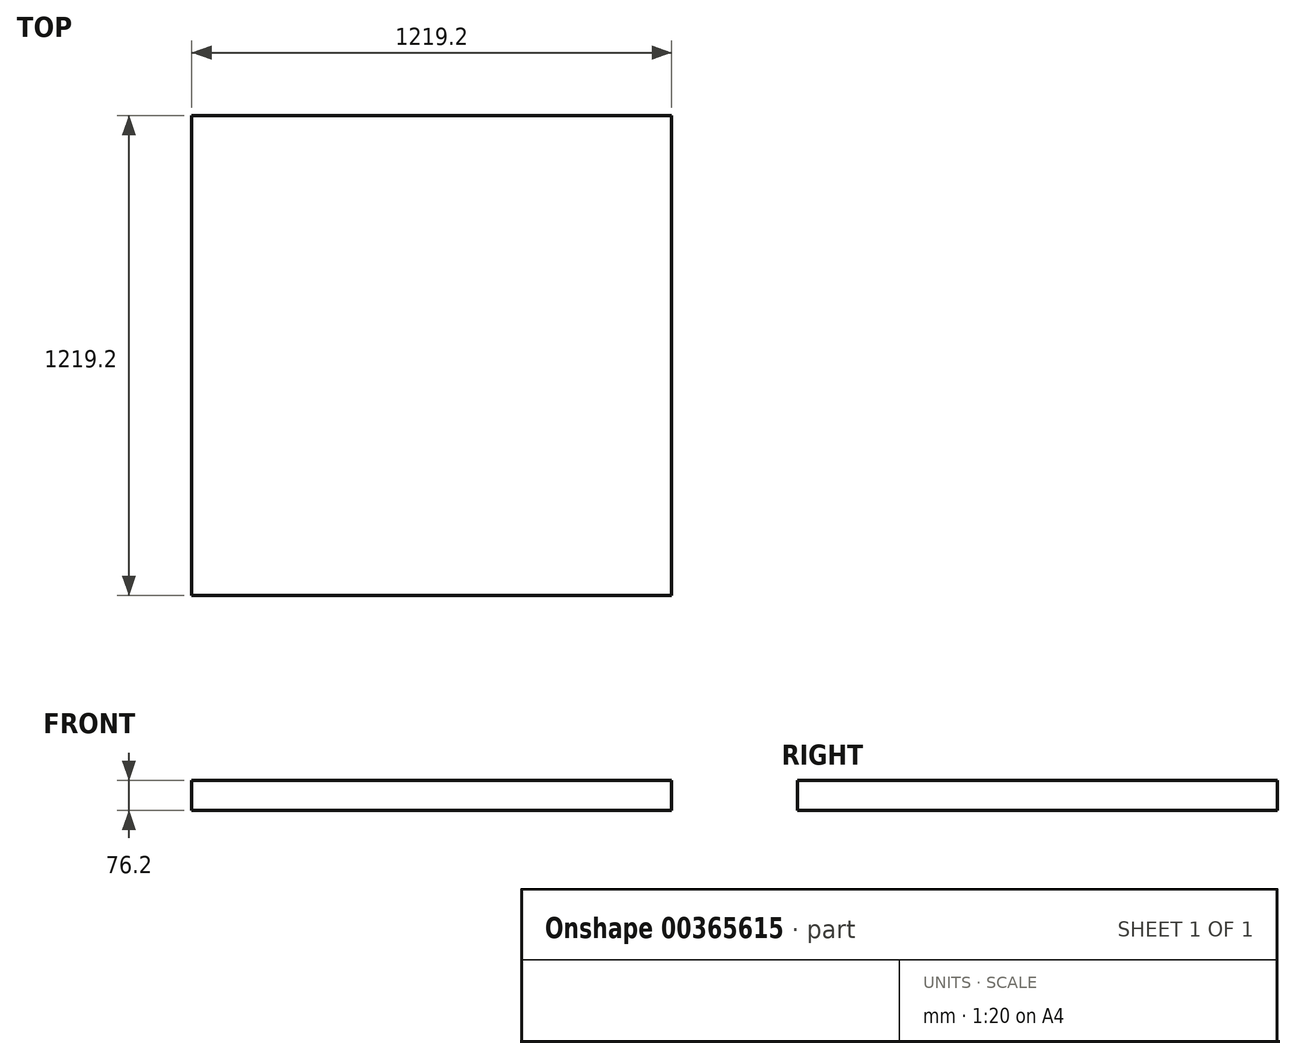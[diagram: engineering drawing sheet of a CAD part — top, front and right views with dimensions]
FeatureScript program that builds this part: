
annotation { "Feature Type Name" : "Feature", "Feature Type Description" : "" }
export const myFeature = defineFeature(function(context is Context, id is Id, definition is map)
    precondition{}
    {
        {
            var Q0;
            Q0=qCreatedBy(makeId("Top.planeOp"),FACE);
            var sketch = newSketch(context, id + "F0", { "sketchPlane" : qUnion([Q0])});
            skLineSegment(sketch, "E0.bottom", {"start": v(609.6, -609.6) * mm, "end": v(-609.6, -609.6) * mm});
            skLineSegment(sketch, "E0.top", {"start": v(609.6, 609.6) * mm, "end": v(-609.6, 609.6) * mm});
            skLineSegment(sketch, "E0.left", {"start": v(609.6, -609.6) * mm, "end": v(609.6, 609.6) * mm});
            skLineSegment(sketch, "E0.right", {"start": v(-609.6, -609.6) * mm, "end": v(-609.6, 609.6) * mm});
            skPoint(sketch, "E0.middle", {"position": v(0, 0) * mm});
            skSolve(sketch);
        }
        {
            var Q0;
            Q0=makeQuery(id+"F0.imprint","IMPRINT",FACE,{"disambiguationData":[TD([[makeQuery(id+"F0.imprint","IMPRINT",EDGE,{"derivedFrom":sQuery(id+"F0.wireOp",EDGE,"E0.bottom")}),-1.0]])]});
            extrude(context, id + "F1", {"entities" : qUnion([Q0]), "oppositeDirection" : true, "depth" : 76.2 * mm, "offsetDistance" : 25.4 * mm});
        }
    });
